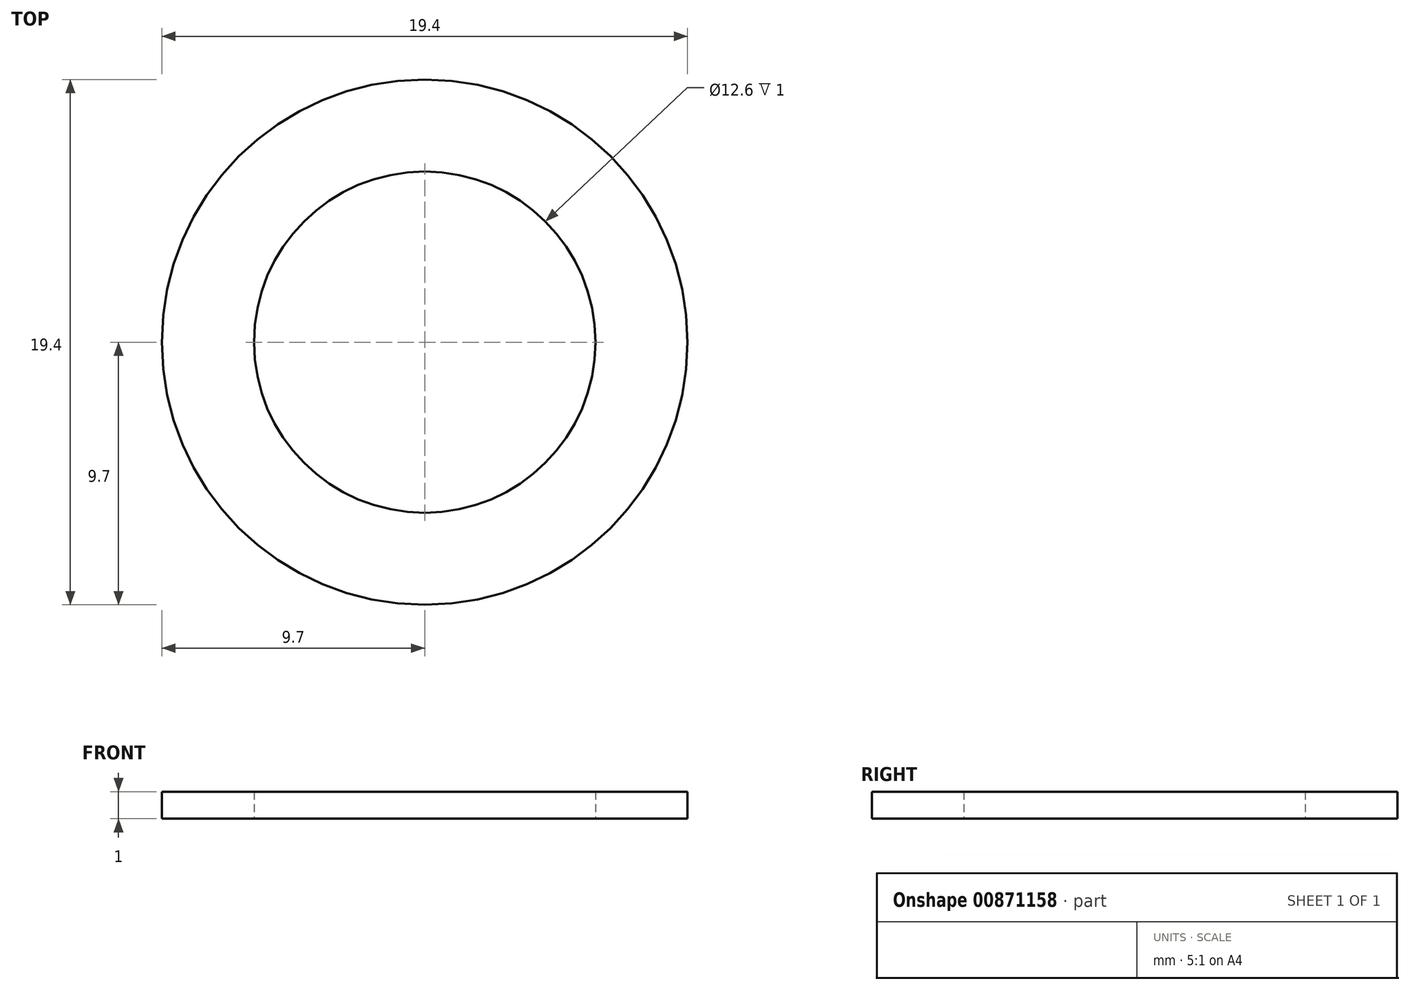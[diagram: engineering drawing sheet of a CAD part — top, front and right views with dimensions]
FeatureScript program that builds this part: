
annotation { "Feature Type Name" : "Feature", "Feature Type Description" : "" }
export const myFeature = defineFeature(function(context is Context, id is Id, definition is map)
    precondition{}
    {
        {
            var Q0;
            Q0=qCreatedBy(makeId("Top.planeOp"),FACE);
            var sketch = newSketch(context, id + "F0", { "sketchPlane" : qUnion([Q0])});
            skCircle(sketch, "E0", {"center": v(0, 0) * mm, "radius": 6.3 * mm});
            skCircle(sketch, "E1", {"center": v(0, 0) * mm, "radius": 9.7 * mm});
            skSolve(sketch);
        }
        {
            var Q0;
            Q0=makeQuery(id+"F0.imprint","IMPRINT",FACE,{"disambiguationData":[TD([[makeQuery(id+"F0.imprint","IMPRINT",EDGE,{"derivedFrom":sQuery(id+"F0.wireOp",EDGE,"E0")}),-1.0]])]});
            extrude(context, id + "F1", {"entities" : qUnion([Q0]), "depth" : 1 * mm, "offsetDistance" : 25 * mm});
        }
    });
